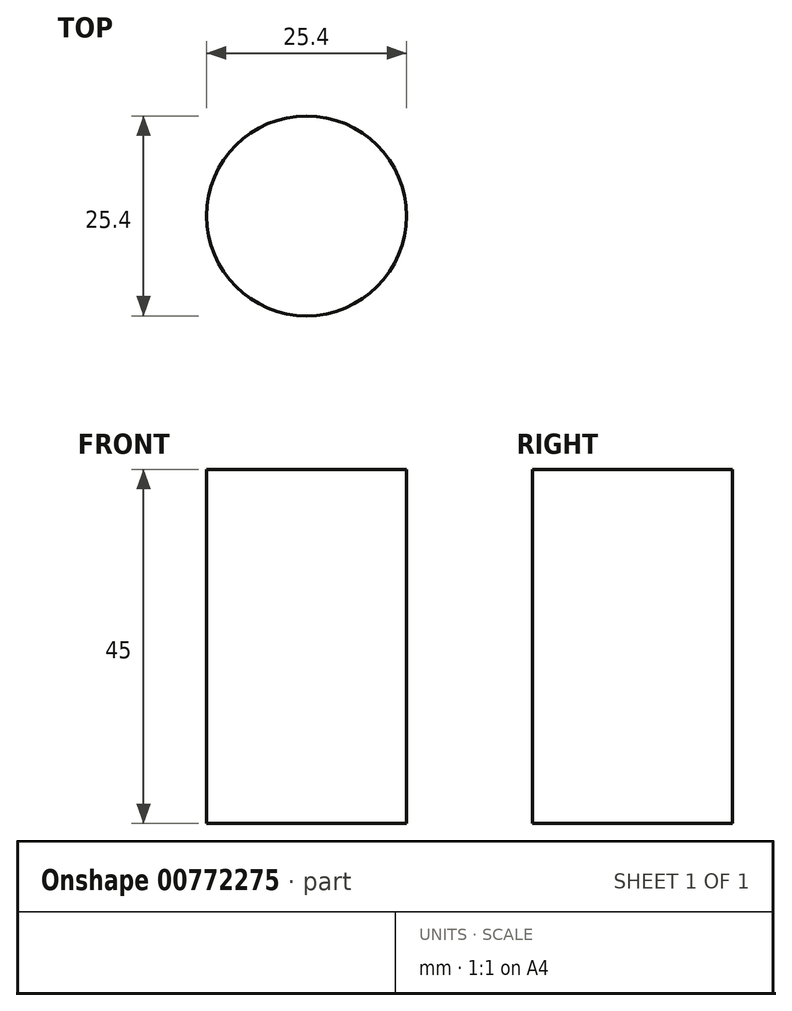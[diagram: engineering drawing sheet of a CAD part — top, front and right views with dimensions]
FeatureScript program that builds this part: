
annotation { "Feature Type Name" : "Feature", "Feature Type Description" : "" }
export const myFeature = defineFeature(function(context is Context, id is Id, definition is map)
    precondition{}
    {
        {
            var Q0;
            Q0=qCreatedBy(makeId("Top.planeOp"),FACE);
            var sketch = newSketch(context, id + "F0", { "sketchPlane" : qUnion([Q0])});
            skCircle(sketch, "E0", {"center": v(0, 0) * mm, "radius": 12.7 * mm});
            skSolve(sketch);
        }
        {
            var Q0;
            Q0 = qSketchRegion(id + "F0", true);
            extrude(context, id + "F1", {"entities" : qUnion([Q0]), "endBound" : BoundingType.SYMMETRIC, "depth" : 45 * mm, "offsetDistance" : 25 * mm});
        }
    });
